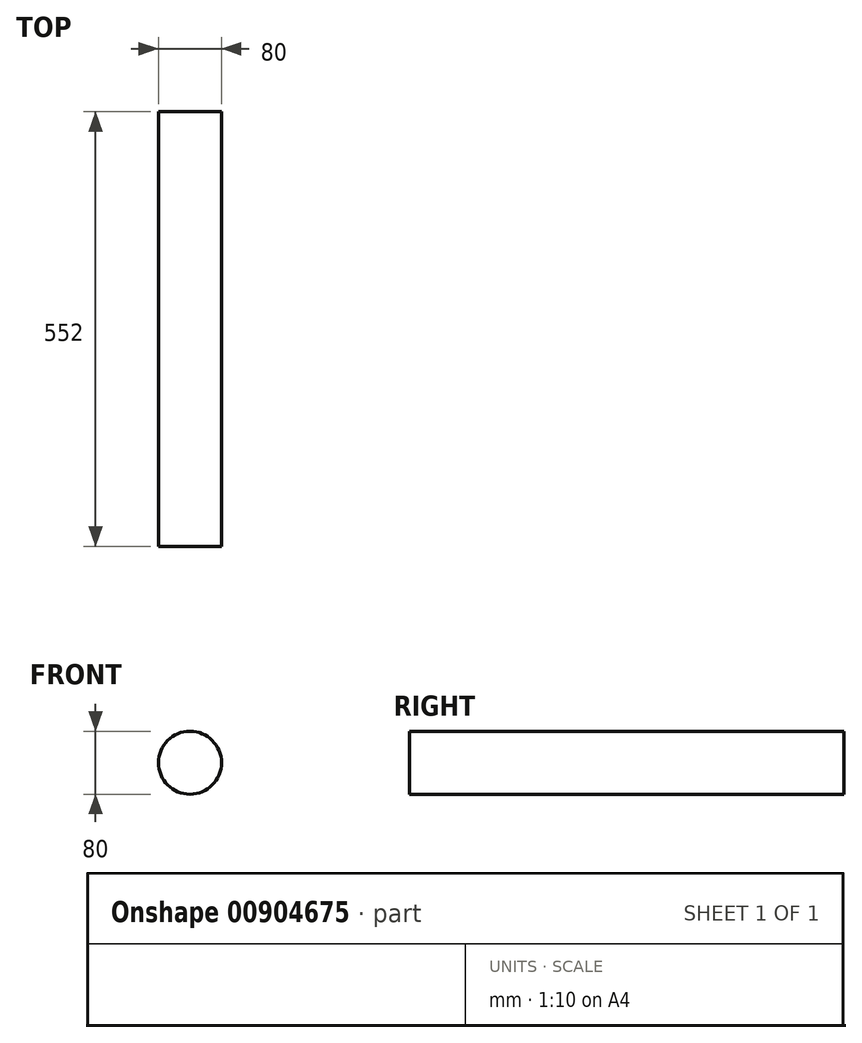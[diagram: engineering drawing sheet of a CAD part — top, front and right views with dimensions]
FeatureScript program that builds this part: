
annotation { "Feature Type Name" : "Feature", "Feature Type Description" : "" }
export const myFeature = defineFeature(function(context is Context, id is Id, definition is map)
    precondition{}
    {
        {
            var Q0;
            Q0=qCreatedBy(makeId("Front.planeOp"),FACE);
            var sketch = newSketch(context, id + "F0", { "sketchPlane" : qUnion([Q0])});
            skCircle(sketch, "E0", {"center": v(1.98, 0) * mm, "radius": 40 * mm});
            skSolve(sketch);
        }
        {
            var Q0;
            Q0 = qSketchRegion(id + "F0", true);
            extrude(context, id + "F1", {"entities" : qUnion([Q0]), "oppositeDirection" : true, "depth" : 552 * mm, "offsetDistance" : 25 * mm});
        }
    });
